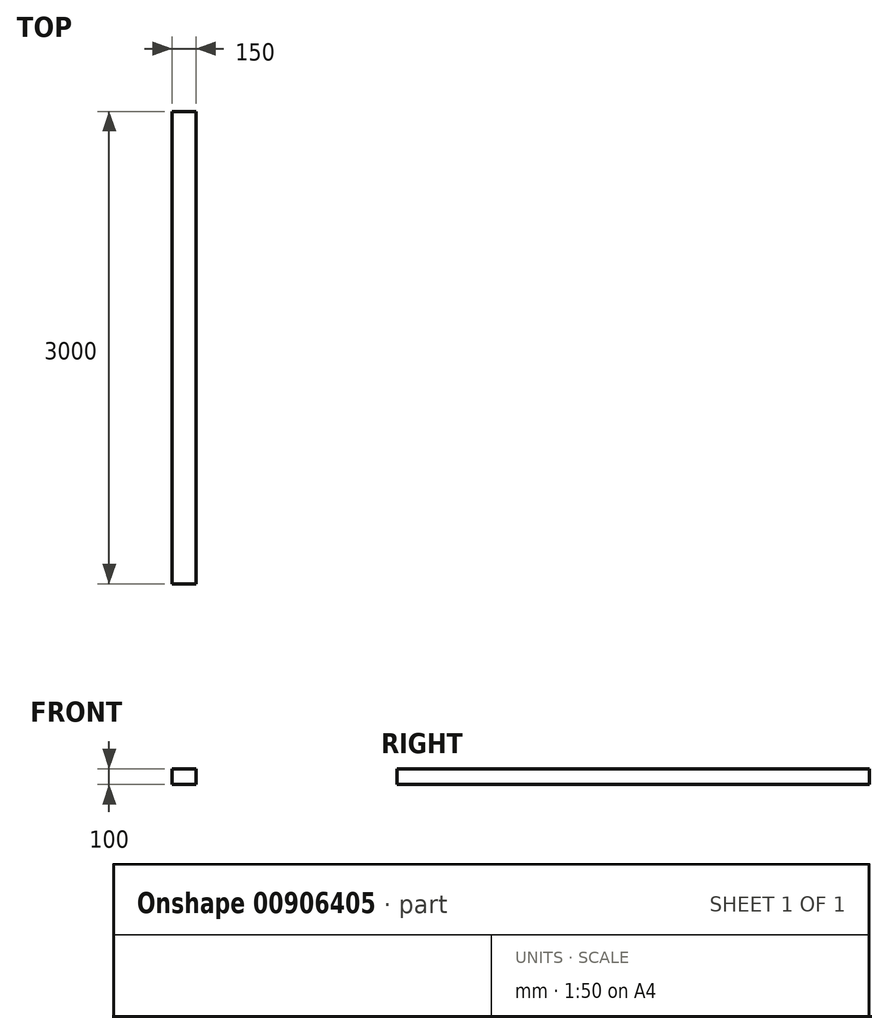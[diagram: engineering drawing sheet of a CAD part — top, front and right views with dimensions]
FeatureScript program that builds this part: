
annotation { "Feature Type Name" : "Feature", "Feature Type Description" : "" }
export const myFeature = defineFeature(function(context is Context, id is Id, definition is map)
    precondition{}
    {
        {
            var Q0;
            Q0=qCreatedBy(makeId("Front.planeOp"),FACE);
            var sketch = newSketch(context, id + "F0", { "sketchPlane" : qUnion([Q0])});
            skLineSegment(sketch, "E0.bottom", {"start": v(0, 0) * mm, "end": v(150, 0) * mm});
            skLineSegment(sketch, "E0.top", {"start": v(0, 100) * mm, "end": v(150, 100) * mm});
            skLineSegment(sketch, "E0.left", {"start": v(0, 0) * mm, "end": v(0, 100) * mm});
            skLineSegment(sketch, "E0.right", {"start": v(150, 0) * mm, "end": v(150, 100) * mm});
            skSolve(sketch);
        }
        {
            var Q0;
            Q0 = qSketchRegion(id + "F0", true);
            extrude(context, id + "F1", {"entities" : qUnion([Q0]), "depth" : 3000 * mm, "offsetDistance" : 25 * mm});
        }
    });
